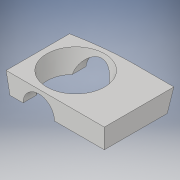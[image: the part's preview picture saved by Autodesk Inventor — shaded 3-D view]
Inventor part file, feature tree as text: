
AUTODESK INVENTOR PART (.ipt)
format: ipt  version: 2018 (Build 220112000, 112)  size: 162,304 bytes
history: native  units: in
note: dims shown in document units (in); Inventor stores cm internally (conversion verified against a paired STEP export)
features: sketch x6, loft x2, extrude x2, plane x1
ambient origin geometry x8: Origin, YZ Plane, XZ Plane, XY Plane, X Axis, Y Axis, Z Axis, Center Point
bodies: Solid1 (feature_tree)
feature tree (11):
  sketch  "Sketch1"  dims[d1=0.8in d2=1.2in]
  plane  "Work Plane1"
  loft  "Loft1"
  loft  "Loft2"
  extrude  "Extrusion1"  Depth=0.875in
  extrude  "Extrusion2"  TaperAngle=0.0deg  [1 undecoded]
  sketch  "Sketch3"  dims[d4=0.4in d5=2.8in]
  sketch  "Sketch4"  dims[d15=0.875in d17=0.875in]
  sketch  "Sketch5"  dims[d18=0.875in d19=0.0in d20=90.0deg]
  sketch  "Sketch6"  dims[d21=0.0in d22=90.0deg]
  sketch  "Sketch7"  dims[d23=1.6in d24=0.875in d26=0.875in d27=0.65in d28=0.0in d29=90.0deg d30=0.0in d31=90.0deg d32=0.4in d33=0.4in d34=0.4in d35=0.2in d36=0.0in d38=3.0in d39=0.0in d40=2.55in d41=0.0in d42=0.0in]
note: 1 required parameter value undecoded (feature->parameter linkage not recoverable at this tier; creation-order binding heuristic only, values carry confidence <= 0.55)
